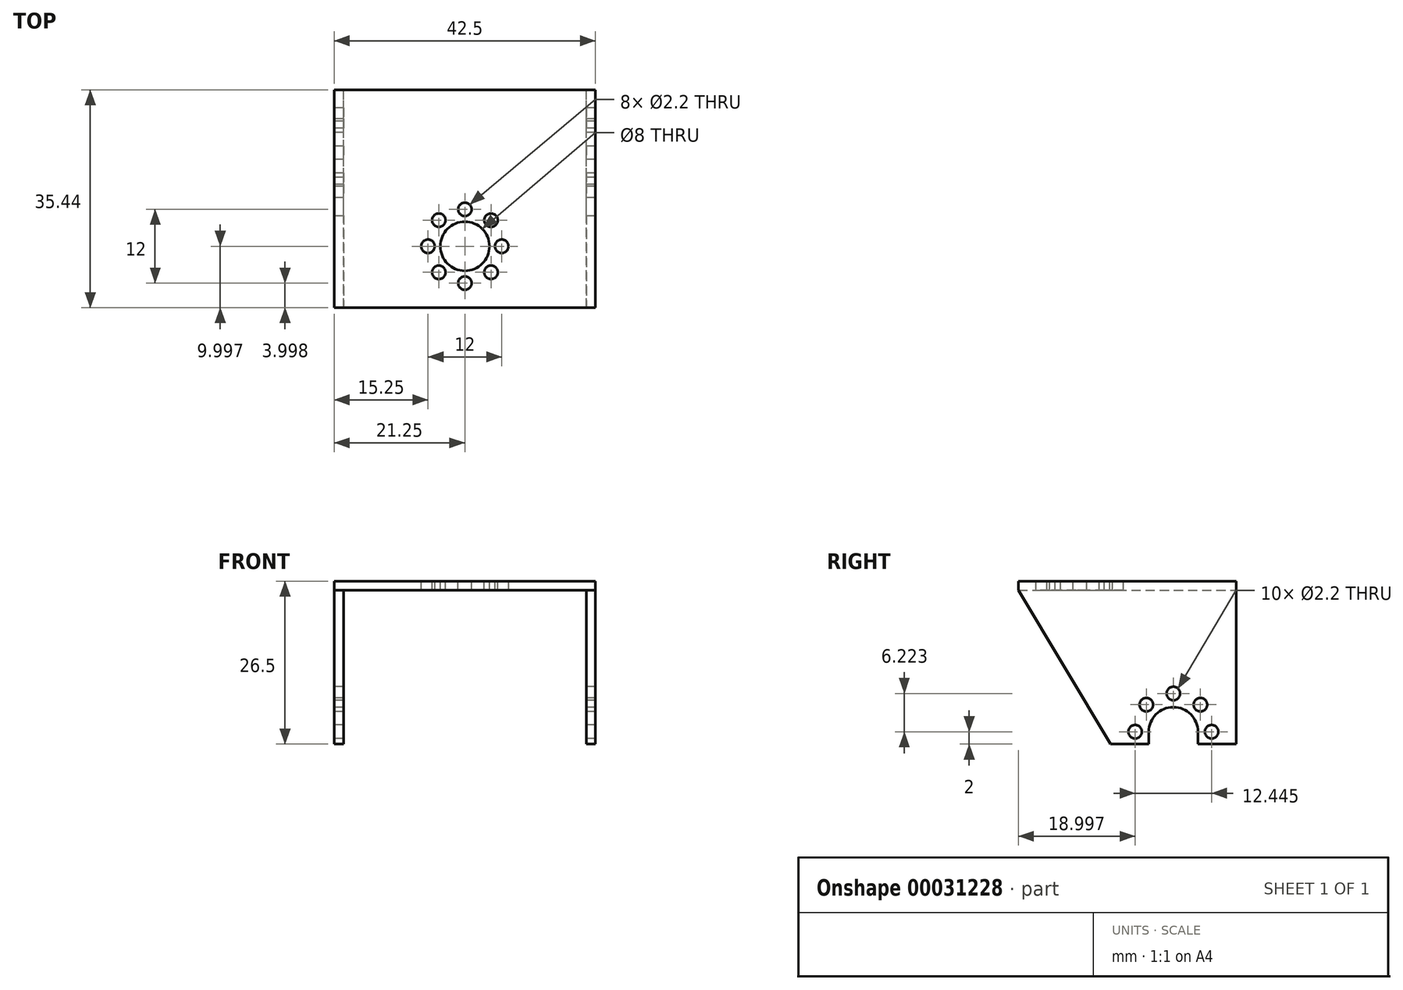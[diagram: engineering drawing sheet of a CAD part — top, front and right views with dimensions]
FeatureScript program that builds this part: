
annotation { "Feature Type Name" : "Feature", "Feature Type Description" : "" }
export const myFeature = defineFeature(function(context is Context, id is Id, definition is map)
    precondition{}
    {
        {
            var Q0;
            Q0=qCreatedBy(makeId("Front.planeOp"),FACE);
            var sketch = newSketch(context, id + "F0", { "sketchPlane" : qUnion([Q0])});
            skLineSegment(sketch, "E0.bottom", {"start": v(0, 0) * mm, "end": v(1.5, 0) * mm});
            skLineSegment(sketch, "E0.top", {"start": v(0, 26.5) * mm, "end": v(42.5, 26.5) * mm});
            skLineSegment(sketch, "E0.left", {"start": v(0, 0) * mm, "end": v(0, 26.5) * mm});
            skLineSegment(sketch, "E0.right", {"start": v(42.5, 0) * mm, "end": v(42.5, 26.5) * mm});
            skLineSegment(sketch, "E1.top", {"start": v(1.5, 25) * mm, "end": v(41, 25) * mm});
            skLineSegment(sketch, "E1.left", {"start": v(1.5, 0) * mm, "end": v(1.5, 25) * mm});
            skLineSegment(sketch, "E1.right", {"start": v(41, 0) * mm, "end": v(41, 25) * mm});
            skLineSegment(sketch, "E2.trimOffspring", {"start": v(41, 0) * mm, "end": v(42.5, 0) * mm});
            skSolve(sketch);
        }
        {
            var Q0;
            Q0=qSketchRegion(id+"F0",true);
            extrude(context, id + "F1", {"entities" : qUnion([Q0]), "depth" : 33 * mm});
        }
        {
            var Q0;
            Q0=makeQuery(id+"F1.opExtrude","SWEPT_FACE",FACE,{"disambiguationData":[OSD([sQuery(id+"F0.wireOp",EDGE,"E0.left")])]});
            var sketch = newSketch(context, id + "F2", { "sketchPlane" : qUnion([Q0])});
            skArc(sketch, "E3", {"start": v(20.5, 2) * mm, "mid": v(16.5, 6) * mm, "end": v(12.5, 2) * mm});
            skCircle(sketch, "E4", {"center": v(22.72, 2) * mm, "radius": 1.1 * mm});
            skCircle(sketch, "E5.1.0", {"center": v(20.9, 6.4) * mm, "radius": 1.1 * mm});
            skCircle(sketch, "E5.2.0", {"center": v(16.5, 8.22) * mm, "radius": 1.1 * mm});
            skCircle(sketch, "E5.3.0", {"center": v(12.1, 6.4) * mm, "radius": 1.1 * mm});
            skCircle(sketch, "E5.4.0", {"center": v(10.28, 2) * mm, "radius": 1.1 * mm});
            skLineSegment(sketch, "E6", {"start": v(12.5, 2) * mm, "end": v(12.5, 0) * mm});
            skLineSegment(sketch, "E7", {"start": v(20.5, 2) * mm, "end": v(20.5, 0) * mm});
            skLineSegment(sketch, "E8", {"start": v(12.5, 0) * mm, "end": v(20.5, 0) * mm});
            skLineSegment(sketch, "E9", {"start": v(16.5, 26.5) * mm, "end": v(16.5, 0) * mm, "construction": true});
            skPoint(sketch, "E10", {"position": v(16.5, 0) * mm});
            skLineSegment(sketch, "E11", {"start": v(6.28, 0) * mm, "end": v(0, 25) * mm});
            skLineSegment(sketch, "E12", {"start": v(6.28, 0) * mm, "end": v(0, 0) * mm});
            skLineSegment(sketch, "E13", {"start": v(0, 0) * mm, "end": v(0, 25) * mm});
            skLineSegment(sketch, "E14.MirrorCS", {"start": v(33, 0) * mm, "end": v(33, 25) * mm});
            skLineSegment(sketch, "E15.MirrorCS", {"start": v(26.72, 0) * mm, "end": v(33, 25) * mm});
            skLineSegment(sketch, "E16.MirrorCS", {"start": v(26.72, 0) * mm, "end": v(33, 0) * mm});
            skLineSegment(sketch, "E17.bottom", {"start": v(33, 0) * mm, "end": v(26.72, 0) * mm});
            skLineSegment(sketch, "E17.top", {"start": v(33, 25) * mm, "end": v(26.72, 25) * mm});
            skLineSegment(sketch, "E17.right", {"start": v(26.72, 0) * mm, "end": v(26.72, 25) * mm});
            skLineSegment(sketch, "E18.MirrorCS", {"start": v(0, 25) * mm, "end": v(6.28, 25) * mm});
            skLineSegment(sketch, "E19.MirrorCS", {"start": v(6.28, 0) * mm, "end": v(6.28, 25) * mm});
            skLineSegment(sketch, "E20.bottom", {"start": v(33, 26.5) * mm, "end": v(26.72, 26.5) * mm});
            skLineSegment(sketch, "E20.left", {"start": v(33, 26.5) * mm, "end": v(33, 25) * mm});
            skLineSegment(sketch, "E20.right", {"start": v(26.72, 26.5) * mm, "end": v(26.72, 25) * mm});
            skLineSegment(sketch, "E21.top", {"start": v(0, 26.5) * mm, "end": v(6.28, 26.5) * mm});
            skLineSegment(sketch, "E21.left", {"start": v(0, 25) * mm, "end": v(0, 26.5) * mm});
            skLineSegment(sketch, "E21.right", {"start": v(6.28, 25) * mm, "end": v(6.28, 26.5) * mm});
            skSolve(sketch);
        }
        {
            var Q0;
            Q0=qSketchRegion(id+"F2",true);
            extrude(context, id + "F3", {"entities" : qUnion([Q0]), "operationType" : NewBodyOperationType.REMOVE, "endBound" : BoundingType.THROUGH_ALL, "oppositeDirection" : true, "depth" : 25 * mm});
        }
        {
            var Q0;
            Q0=makeQuery(id+"F3.boolean.opBoolean","COPY",FACE,{"derivedFrom":makeQuery(id+"F3.opExtrude","SWEPT_FACE",FACE,{"disambiguationData":[OSD([sQuery(id+"F2.wireOp",EDGE,"E17.right"),sQuery(id+"F2.wireOp",EDGE,"E20.right")])]})});
            var sketch = newSketch(context, id + "F4", { "sketchPlane" : qUnion([Q0])});
            skLineSegment(sketch, "E22.0", {"start": v(1.5, 25) * mm, "end": v(1.5, 0) * mm});
            skLineSegment(sketch, "E23.0", {"start": v(0, 26.5) * mm, "end": v(0, 0) * mm});
            skLineSegment(sketch, "E24.0", {"start": v(42.5, 26.5) * mm, "end": v(0, 26.5) * mm});
            skLineSegment(sketch, "E25.0", {"start": v(42.5, 26.5) * mm, "end": v(42.5, 0) * mm});
            skLineSegment(sketch, "E26.0", {"start": v(41, 25) * mm, "end": v(1.5, 25) * mm});
            skLineSegment(sketch, "E27.0", {"start": v(41, 25) * mm, "end": v(41, 0) * mm});
            skLineSegment(sketch, "E28.0", {"start": v(1.5, 0) * mm, "end": v(0, 0) * mm});
            skLineSegment(sketch, "E29.0", {"start": v(42.5, 0) * mm, "end": v(41, 0) * mm});
            skSolve(sketch);
        }
        {
            var Q0;
            Q0 = qSketchRegion(id + "F4", true);
            extrude(context, id + "F5", {"entities" : qUnion([Q0]), "operationType" : NewBodyOperationType.ADD, "depth" : 15 * mm});
        }
        {
            var Q0;
            Q0=makeQuery(id+"F5.boolean.opBoolean","MERGE",FACE,{"derivedFrom":[makeQuery(id+"F1.opExtrude","SWEPT_FACE",FACE,{"disambiguationData":[OSD([sQuery(id+"F0.wireOp",EDGE,"E0.right")])]}),makeQuery(id+"F5.opExtrude","SWEPT_FACE",FACE,{"disambiguationData":[OSD([sQuery(id+"F4.wireOp",EDGE,"E25.0")])]})]});
            var sketch = newSketch(context, id + "F6", { "sketchPlane" : qUnion([Q0])});
            skLineSegment(sketch, "E30", {"start": v(-41.72, 25) * mm, "end": v(-26.72, 0) * mm});
            skPoint(sketch, "E31", {"position": v(-22.72, 2) * mm});
            skPoint(sketch, "E32", {"position": v(-10.28, 2) * mm});
            skSolve(sketch);
        }
        {
            var Q0;
            Q0 = qSketchRegion(id + "F6", true);
            var Q1;
            {var subQ0=sQuery(id+"F6.wireOp",EDGE,"E30");Q1=makeQuery(id+"F6.imprint","IMPRINT",FACE,{"disambiguationData":[TD([[makeQuery(id+"F6.imprint","IMPRINT",EDGE,{"derivedFrom":subQ0}),-1.0]])]});}
            extrude(context, id + "F7", {"entities" : qUnion([Q0, Q1]), "operationType" : NewBodyOperationType.REMOVE, "endBound" : BoundingType.THROUGH_ALL, "oppositeDirection" : true, "depth" : 25 * mm});
        }
        {
            var Q0;
            Q0=makeQuery(id+"F5.boolean.opBoolean","MERGE",FACE,{"derivedFrom":[makeQuery(id+"F1.opExtrude","SWEPT_FACE",FACE,{"disambiguationData":[OSD([sQuery(id+"F0.wireOp",EDGE,"E0.top")])]}),makeQuery(id+"F5.opExtrude","SWEPT_FACE",FACE,{"disambiguationData":[OSD([sQuery(id+"F4.wireOp",EDGE,"E24.0")])]})]});
            var sketch = newSketch(context, id + "F8", { "sketchPlane" : qUnion([Q0])});
            skLineSegment(sketch, "E33", {"start": v(21.25, -6.28) * mm, "end": v(21.25, -41.72) * mm, "construction": true});
            skCircle(sketch, "E34", {"center": v(21.25, -31.72) * mm, "radius": 4 * mm});
            skCircle(sketch, "E35", {"center": v(21.25, -37.72) * mm, "radius": 1.1 * mm});
            skCircle(sketch, "E36.1.0", {"center": v(25.5, -35.97) * mm, "radius": 1.1 * mm});
            skCircle(sketch, "E36.2.0", {"center": v(27.25, -31.72) * mm, "radius": 1.1 * mm});
            skCircle(sketch, "E36.3.0", {"center": v(25.5, -27.48) * mm, "radius": 1.1 * mm});
            skCircle(sketch, "E36.4.0", {"center": v(21.25, -25.72) * mm, "radius": 1.1 * mm});
            skCircle(sketch, "E36.5.0", {"center": v(17, -27.48) * mm, "radius": 1.1 * mm});
            skCircle(sketch, "E36.6.0", {"center": v(15.25, -31.72) * mm, "radius": 1.1 * mm});
            skCircle(sketch, "E36.7.0", {"center": v(17, -35.97) * mm, "radius": 1.1 * mm});
            skSolve(sketch);
        }
        {
            var Q0;
            Q0 = qSketchRegion(id + "F8", true);
            extrude(context, id + "F9", {"entities" : qUnion([Q0]), "operationType" : NewBodyOperationType.REMOVE, "endBound" : BoundingType.UP_TO_NEXT, "oppositeDirection" : true, "depth" : 25 * mm});
        }
    });
